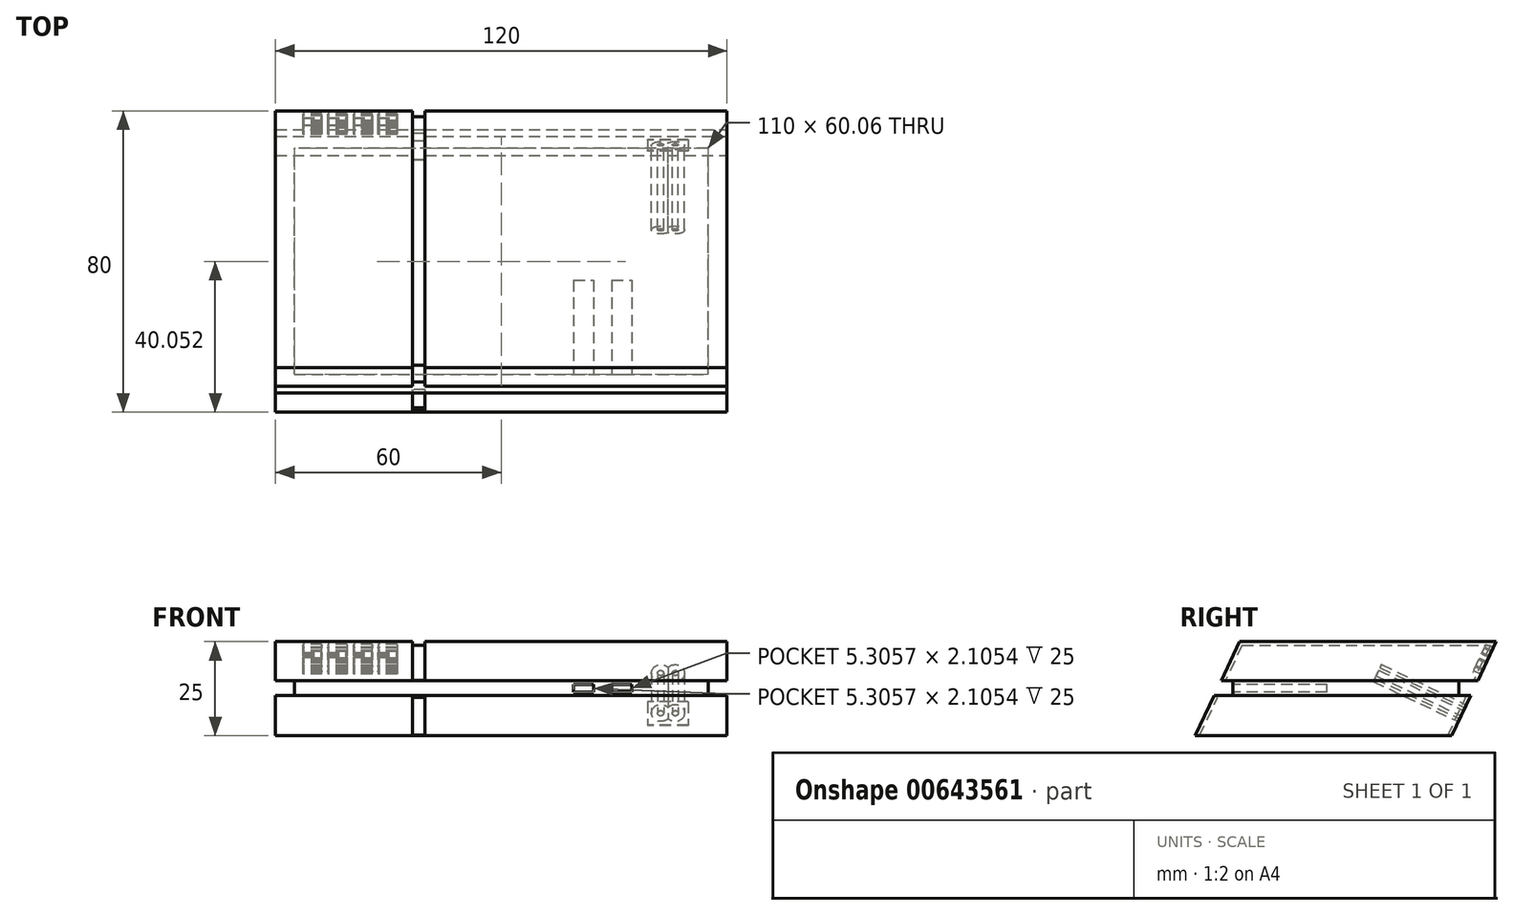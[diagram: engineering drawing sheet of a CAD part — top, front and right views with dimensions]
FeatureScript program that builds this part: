
annotation { "Feature Type Name" : "Feature", "Feature Type Description" : "" }
export const myFeature = defineFeature(function(context is Context, id is Id, definition is map)
    precondition{}
    {
        {
            var Q0;
            Q0=qCreatedBy(makeId("Top.planeOp"),FACE);
            var sketch = newSketch(context, id + "F0", { "sketchPlane" : qUnion([Q0])});
            skLineSegment(sketch, "E0.bottom", {"start": v(60, -40) * mm, "end": v(-60, -40) * mm});
            skLineSegment(sketch, "E0.top", {"start": v(60, 40) * mm, "end": v(-60, 40) * mm});
            skLineSegment(sketch, "E0.left", {"start": v(60, -40) * mm, "end": v(60, 40) * mm});
            skLineSegment(sketch, "E0.right", {"start": v(-60, -40) * mm, "end": v(-60, 40) * mm});
            skPoint(sketch, "E0.middle", {"position": v(0, 0) * mm});
            skSolve(sketch);
        }
        {
            var Q0;
            Q0=makeQuery(id+"F0.imprint","IMPRINT",FACE,{"disambiguationData":[TD([[makeQuery(id+"F0.imprint","IMPRINT",EDGE,{"derivedFrom":sQuery(id+"F0.wireOp",EDGE,"E0.bottom")}),-1.0]])]});
            extrude(context, id + "F1", {"entities" : qUnion([Q0]), "depth" : 25 * mm, "offsetDistance" : 25 * mm});
        }
        {
            var Q0;
            Q0=makeQuery(id+"F1.opExtrude","SWEPT_FACE",FACE,{"disambiguationData":[OSD([sQuery(id+"F0.wireOp",EDGE,"E0.left")])]});
            var sketch = newSketch(context, id + "F2", { "sketchPlane" : qUnion([Q0])});
            skLineSegment(sketch, "E1", {"start": v(-28.19, 25) * mm, "end": v(-40, 0) * mm});
            skSolve(sketch);
        }
        {
            var Q0;
            {var subQ0=sQuery(id+"F2.wireOp",EDGE,"E1");Q0=makeQuery(id+"F2.imprint","IMPRINT",FACE,{"disambiguationData":[TD([[makeQuery(id+"F2.imprint","IMPRINT",EDGE,{"derivedFrom":subQ0}),-1.0]])]});}
            extrude(context, id + "F3", {"entities" : qUnion([Q0]), "operationType" : NewBodyOperationType.REMOVE, "endBound" : BoundingType.THROUGH_ALL, "oppositeDirection" : true, "depth" : 25 * mm, "offsetDistance" : 25 * mm});
        }
        {
            var Q0;
            Q0=makeQuery(id+"F1.opExtrude","SWEPT_FACE",FACE,{"disambiguationData":[OSD([sQuery(id+"F0.wireOp",EDGE,"E0.left")])]});
            var sketch = newSketch(context, id + "F4", { "sketchPlane" : qUnion([Q0])});
            skLineSegment(sketch, "E2", {"start": v(40, 25) * mm, "end": v(28.19, 0) * mm});
            skSolve(sketch);
        }
        {
            var Q0;
            {var subQ0=sQuery(id+"F4.wireOp",EDGE,"E2");Q0=makeQuery(id+"F4.imprint","IMPRINT",FACE,{"disambiguationData":[TD([[makeQuery(id+"F4.imprint","IMPRINT",EDGE,{"derivedFrom":subQ0}),1.0]])]});}
            extrude(context, id + "F5", {"entities" : qUnion([Q0]), "operationType" : NewBodyOperationType.REMOVE, "endBound" : BoundingType.THROUGH_ALL, "oppositeDirection" : true, "depth" : 25 * mm, "offsetDistance" : 25 * mm});
        }
        {
            var Q0;
            Q0=makeQuery(id+"F1.opExtrude","SWEPT_FACE",FACE,{"disambiguationData":[OSD([sQuery(id+"F0.wireOp",EDGE,"E0.left")])]});
            var sketch = newSketch(context, id + "F6", { "sketchPlane" : qUnion([Q0])});
            skLineSegment(sketch, "E3.bottom", {"start": v(-40.65, 14.59) * mm, "end": v(40.65, 14.59) * mm});
            skLineSegment(sketch, "E3.top", {"start": v(-40.65, 10.62) * mm, "end": v(40.65, 10.62) * mm});
            skLineSegment(sketch, "E3.left", {"start": v(-40.65, 14.59) * mm, "end": v(-40.65, 10.62) * mm});
            skLineSegment(sketch, "E3.right", {"start": v(40.65, 14.59) * mm, "end": v(40.65, 10.62) * mm});
            skPoint(sketch, "E3.middle", {"position": v(0, 12.6) * mm});
            skSolve(sketch);
        }
        {
            var Q0;
            {var subQ0=sQuery(id+"F6.wireOp",EDGE,"E3.bottom");var subQ1=makeQuery(id+"F3.boolean.opBoolean","COPY",EDGE,{"derivedFrom":makeQuery(id+"F3.opExtrude","CAP_EDGE",EDGE,{"disambiguationData":[OSD([sQuery(id+"F2.wireOp",EDGE,"E1")])],"isStart":true})});var subQ2=makeQuery(id+"F6.imprint","INTERSECT",VERTEX,{"derivedFrom":[subQ1,subQ0]});Q0=makeQuery(id+"F6.imprint","IMPRINT",FACE,{"disambiguationData":[TD([[makeQuery(id+"F6.imprint","IMPRINT",EDGE,{"disambiguationData":[TD([[subQ2,-1.0]])],"derivedFrom":subQ0}),-1.0]])]});}
            extrude(context, id + "F7", {"entities" : qUnion([Q0]), "operationType" : NewBodyOperationType.REMOVE, "oppositeDirection" : true, "depth" : 5 * mm, "offsetDistance" : 25 * mm});
        }
        {
            var Q0;
            Q0=makeQuery(id+"F7.boolean.opBoolean","COPY",FACE,{"derivedFrom":makeQuery(id+"F7.opExtrude","CAP_FACE",FACE,{"disambiguationData":[OSD([sQuery(id+"F2.wireOp",EDGE,"E1"),sQuery(id+"F4.wireOp",EDGE,"E2"),sQuery(id+"F6.wireOp",EDGE,"E3.bottom"),sQuery(id+"F6.wireOp",EDGE,"E3.top")])],"isStart":false})});
            var sketch = newSketch(context, id + "F8", { "sketchPlane" : qUnion([Q0])});
            skLineSegment(sketch, "E4.bottom", {"start": v(-34.98, 10.62) * mm, "end": v(-29.98, 10.62) * mm});
            skLineSegment(sketch, "E4.top", {"start": v(-34.98, 14.59) * mm, "end": v(-29.98, 14.59) * mm});
            skLineSegment(sketch, "E4.left", {"start": v(-34.98, 10.62) * mm, "end": v(-34.98, 14.59) * mm});
            skLineSegment(sketch, "E4.right", {"start": v(-29.98, 10.62) * mm, "end": v(-29.98, 14.59) * mm});
            skSolve(sketch);
        }
        {
            var Q0;
            Q0=makeQuery(id+"F8.imprint","IMPRINT",FACE,{"disambiguationData":[TD([[makeQuery(id+"F8.imprint","IMPRINT",EDGE,{"derivedFrom":sQuery(id+"F8.wireOp",EDGE,"E4.bottom")}),1.0]])]});
            extrude(context, id + "F9", {"entities" : qUnion([Q0]), "operationType" : NewBodyOperationType.REMOVE, "oppositeDirection" : true, "depth" : 150 * mm, "offsetDistance" : 25 * mm});
        }
        {
            var Q0;
            Q0=makeQuery(id+"F1.opExtrude","SWEPT_FACE",FACE,{"disambiguationData":[OSD([sQuery(id+"F0.wireOp",EDGE,"E0.right")])]});
            var sketch = newSketch(context, id + "F10", { "sketchPlane" : qUnion([Q0])});
            skLineSegment(sketch, "E5.bottom", {"start": v(29.98, 14.59) * mm, "end": v(-38.1, 14.59) * mm});
            skLineSegment(sketch, "E5.top", {"start": v(29.98, 10.62) * mm, "end": v(-38.1, 10.62) * mm});
            skLineSegment(sketch, "E5.left", {"start": v(29.98, 14.59) * mm, "end": v(29.98, 10.62) * mm});
            skLineSegment(sketch, "E5.right", {"start": v(-38.1, 14.59) * mm, "end": v(-38.1, 10.62) * mm});
            skSolve(sketch);
        }
        {
            var Q0;
            {var subQ0=sQuery(id+"F10.wireOp",EDGE,"E5.left");Q0=makeQuery(id+"F10.imprint","IMPRINT",FACE,{"disambiguationData":[TD([[makeQuery(id+"F10.imprint","IMPRINT",EDGE,{"derivedFrom":subQ0}),-1.0]])]});}
            extrude(context, id + "F11", {"entities" : qUnion([Q0]), "operationType" : NewBodyOperationType.REMOVE, "oppositeDirection" : true, "depth" : 5 * mm, "offsetDistance" : 25 * mm});
        }
        {
            var Q0;
            Q0=makeQuery(id+"F11.boolean.opBoolean","COPY",FACE,{"derivedFrom":makeQuery(id+"F11.opExtrude","CAP_FACE",FACE,{"disambiguationData":[OSD([sQuery(id+"F0.wireOp",EDGE,"E0.right"),sQuery(id+"F4.wireOp",EDGE,"E2"),sQuery(id+"F10.wireOp",EDGE,"E5.bottom"),sQuery(id+"F10.wireOp",EDGE,"E5.top"),sQuery(id+"F10.wireOp",EDGE,"E5.left")])],"isStart":false})});
            var sketch = newSketch(context, id + "F12", { "sketchPlane" : qUnion([Q0])});
            skLineSegment(sketch, "E6.bottom", {"start": v(-35.08, 14.59) * mm, "end": v(-30.08, 14.59) * mm});
            skLineSegment(sketch, "E6.top", {"start": v(-35.08, 10.62) * mm, "end": v(-30.08, 10.62) * mm});
            skLineSegment(sketch, "E6.left", {"start": v(-35.08, 14.59) * mm, "end": v(-35.08, 10.62) * mm});
            skLineSegment(sketch, "E6.right", {"start": v(-30.08, 14.59) * mm, "end": v(-30.08, 10.62) * mm});
            skSolve(sketch);
        }
        {
            var Q0;
            Q0=makeQuery(id+"F12.imprint","IMPRINT",FACE,{"disambiguationData":[TD([[makeQuery(id+"F12.imprint","IMPRINT",EDGE,{"derivedFrom":sQuery(id+"F12.wireOp",EDGE,"E6.bottom")}),1.0]])]});
            extrude(context, id + "F13", {"entities" : qUnion([Q0]), "operationType" : NewBodyOperationType.REMOVE, "oppositeDirection" : true, "depth" : 170 * mm, "offsetDistance" : 25 * mm});
        }
        {
            var Q0;
            Q0=makeQuery(id+"F9.boolean.opBoolean","SPLIT",FACE,{"disambiguationData":[TD([makeQuery(id+"F7.boolean.opBoolean","COPY",FACE,{"derivedFrom":makeQuery(id+"F7.opExtrude","SWEPT_FACE",FACE,{"disambiguationData":[OSD([sQuery(id+"F6.wireOp",EDGE,"E3.bottom")])]})})])],"derivedFrom":makeQuery(id+"F3.boolean.opBoolean","COPY",FACE,{"derivedFrom":makeQuery(id+"F3.opExtrude","SWEPT_FACE",FACE,{"disambiguationData":[OSD([sQuery(id+"F2.wireOp",EDGE,"E1")])]})})});
            var sketch = newSketch(context, id + "F14", { "sketchPlane" : qUnion([Q0])});
            skLineSegment(sketch, "E7.bottom", {"start": v(-23.65, 10.56) * mm, "end": v(-20.25, 10.56) * mm});
            skLineSegment(sketch, "E7.top", {"start": v(-23.65, -0.96) * mm, "end": v(-20.25, -0.96) * mm});
            skLineSegment(sketch, "E7.left", {"start": v(-23.65, 10.56) * mm, "end": v(-23.65, -0.96) * mm});
            skLineSegment(sketch, "E7.right", {"start": v(-20.25, 10.56) * mm, "end": v(-20.25, -0.96) * mm});
            skLineSegment(sketch, "E8.bottom", {"start": v(-20.25, -16.93) * mm, "end": v(-23.65, -16.93) * mm});
            skLineSegment(sketch, "E8.top", {"start": v(-20.25, -5.34) * mm, "end": v(-23.65, -5.34) * mm});
            skLineSegment(sketch, "E8.left", {"start": v(-20.25, -16.93) * mm, "end": v(-20.25, -5.34) * mm});
            skLineSegment(sketch, "E8.right", {"start": v(-23.65, -16.93) * mm, "end": v(-23.65, -5.34) * mm});
            skSolve(sketch);
        }
        {
            var Q0;
            Q0=makeQuery(id+"F14.imprint","IMPRINT",FACE,{"disambiguationData":[TD([[makeQuery(id+"F14.imprint","IMPRINT",EDGE,{"derivedFrom":sQuery(id+"F14.wireOp",EDGE,"E7.bottom")}),-1.0]])]});
            var Q1;
            Q1=makeQuery(id+"F14.imprint","IMPRINT",FACE,{"disambiguationData":[TD([[makeQuery(id+"F14.imprint","IMPRINT",EDGE,{"derivedFrom":sQuery(id+"F14.wireOp",EDGE,"E8.bottom")}),-1.0]])]});
            extrude(context, id + "F15", {"entities" : qUnion([Q0, Q1]), "operationType" : NewBodyOperationType.REMOVE, "oppositeDirection" : true, "depth" : 1 * mm, "offsetDistance" : 25 * mm});
        }
        {
            var Q0;
            Q0=makeQuery(id+"F1.opExtrude","CAP_FACE",FACE,{"disambiguationData":[OSD([sQuery(id+"F0.wireOp",EDGE,"E0.bottom"),sQuery(id+"F0.wireOp",EDGE,"E0.top"),sQuery(id+"F0.wireOp",EDGE,"E0.left"),sQuery(id+"F0.wireOp",EDGE,"E0.right")])],"isStart":false});
            var sketch = newSketch(context, id + "F16", { "sketchPlane" : qUnion([Q0])});
            skLineSegment(sketch, "E9.bottom", {"start": v(-23.65, -28.19) * mm, "end": v(-20.25, -28.19) * mm});
            skLineSegment(sketch, "E9.top", {"start": v(-23.65, 40) * mm, "end": v(-20.25, 40) * mm});
            skLineSegment(sketch, "E9.left", {"start": v(-23.65, -28.19) * mm, "end": v(-23.65, 40) * mm});
            skLineSegment(sketch, "E9.right", {"start": v(-20.25, -28.19) * mm, "end": v(-20.25, 40) * mm});
            skSolve(sketch);
        }
        {
            var Q0;
            Q0=makeQuery(id+"F16.imprint","IMPRINT",FACE,{"disambiguationData":[TD([[makeQuery(id+"F16.imprint","IMPRINT",EDGE,{"derivedFrom":sQuery(id+"F16.wireOp",EDGE,"E9.bottom")}),1.0]])]});
            extrude(context, id + "F17", {"entities" : qUnion([Q0]), "operationType" : NewBodyOperationType.REMOVE, "oppositeDirection" : true, "depth" : 1 * mm, "offsetDistance" : 25 * mm});
        }
        {
            var Q0;
            Q0=makeQuery(id+"F13.boolean.opBoolean","SPLIT",FACE,{"disambiguationData":[TD([makeQuery(id+"F7.boolean.opBoolean","COPY",FACE,{"derivedFrom":makeQuery(id+"F7.opExtrude","SWEPT_FACE",FACE,{"disambiguationData":[OSD([sQuery(id+"F6.wireOp",EDGE,"E3.bottom")])]})})])],"derivedFrom":makeQuery(id+"F5.boolean.opBoolean","COPY",FACE,{"derivedFrom":makeQuery(id+"F5.opExtrude","SWEPT_FACE",FACE,{"disambiguationData":[OSD([sQuery(id+"F4.wireOp",EDGE,"E2")])]})})});
            var sketch = newSketch(context, id + "F18", { "sketchPlane" : qUnion([Q0])});
            skLineSegment(sketch, "E10.bottom", {"start": v(20.25, 39.7) * mm, "end": v(23.65, 39.7) * mm});
            skLineSegment(sketch, "E10.top", {"start": v(20.25, 28.18) * mm, "end": v(23.65, 28.18) * mm});
            skLineSegment(sketch, "E10.left", {"start": v(20.25, 39.7) * mm, "end": v(20.25, 28.18) * mm});
            skLineSegment(sketch, "E10.right", {"start": v(23.65, 39.7) * mm, "end": v(23.65, 28.18) * mm});
            skLineSegment(sketch, "E11.bottom", {"start": v(23.65, 11.57) * mm, "end": v(20.25, 11.57) * mm});
            skLineSegment(sketch, "E11.top", {"start": v(23.65, 23.8) * mm, "end": v(20.25, 23.8) * mm});
            skLineSegment(sketch, "E11.left", {"start": v(23.65, 11.57) * mm, "end": v(23.65, 23.8) * mm});
            skLineSegment(sketch, "E11.right", {"start": v(20.25, 11.57) * mm, "end": v(20.25, 23.8) * mm});
            skSolve(sketch);
        }
        {
            var Q0;
            {var subQ0=sQuery(id+"F18.wireOp",EDGE,"E10.top");Q0=makeQuery(id+"F18.imprint","IMPRINT",FACE,{"disambiguationData":[TD([[makeQuery(id+"F18.imprint","IMPRINT",EDGE,{"derivedFrom":subQ0}),-1.0]])]});}
            var Q1;
            Q1=makeQuery(id+"F18.imprint","IMPRINT",FACE,{"disambiguationData":[TD([[makeQuery(id+"F18.imprint","IMPRINT",EDGE,{"derivedFrom":sQuery(id+"F18.wireOp",EDGE,"E11.bottom")}),-1.0]])]});
            extrude(context, id + "F19", {"entities" : qUnion([Q0, Q1]), "operationType" : NewBodyOperationType.REMOVE, "oppositeDirection" : true, "depth" : 1 * mm, "offsetDistance" : 25 * mm});
        }
        {
            var Q0;
            Q0=makeQuery(id+"F9.boolean.opBoolean","COPY",FACE,{"derivedFrom":makeQuery(id+"F9.opExtrude","SWEPT_FACE",FACE,{"disambiguationData":[OSD([sQuery(id+"F8.wireOp",EDGE,"E4.right")])]})});
            var sketch = newSketch(context, id + "F20", { "sketchPlane" : qUnion([Q0])});
            skLineSegment(sketch, "E12.bottom", {"start": v(19.23, 13.64) * mm, "end": v(24.53, 13.64) * mm});
            skLineSegment(sketch, "E12.top", {"start": v(19.23, 11.53) * mm, "end": v(24.53, 11.53) * mm});
            skLineSegment(sketch, "E12.left", {"start": v(19.23, 13.64) * mm, "end": v(19.23, 11.53) * mm});
            skLineSegment(sketch, "E12.right", {"start": v(24.53, 13.64) * mm, "end": v(24.53, 11.53) * mm});
            skLineSegment(sketch, "E13.bottom", {"start": v(29.42, 11.53) * mm, "end": v(34.72, 11.53) * mm});
            skLineSegment(sketch, "E13.top", {"start": v(29.42, 13.64) * mm, "end": v(34.72, 13.64) * mm});
            skLineSegment(sketch, "E13.left", {"start": v(29.42, 11.53) * mm, "end": v(29.42, 13.64) * mm});
            skLineSegment(sketch, "E13.right", {"start": v(34.72, 11.53) * mm, "end": v(34.72, 13.64) * mm});
            skSolve(sketch);
        }
        {
            var Q0;
            Q0=makeQuery(id+"F20.imprint","IMPRINT",FACE,{"disambiguationData":[TD([[makeQuery(id+"F20.imprint","IMPRINT",EDGE,{"derivedFrom":sQuery(id+"F20.wireOp",EDGE,"E12.bottom")}),-1.0]])]});
            var Q1;
            Q1=makeQuery(id+"F20.imprint","IMPRINT",FACE,{"disambiguationData":[TD([[makeQuery(id+"F20.imprint","IMPRINT",EDGE,{"derivedFrom":sQuery(id+"F20.wireOp",EDGE,"E13.bottom")}),1.0]])]});
            extrude(context, id + "F21", {"entities" : qUnion([Q0, Q1]), "operationType" : NewBodyOperationType.REMOVE, "oppositeDirection" : true, "depth" : 25 * mm, "offsetDistance" : 25 * mm});
        }
        {
            var Q0;
            {var subQ1=makeQuery(id+"F7.boolean.opBoolean","COPY",FACE,{"derivedFrom":makeQuery(id+"F7.opExtrude","SWEPT_FACE",FACE,{"disambiguationData":[OSD([sQuery(id+"F6.wireOp",EDGE,"E3.top")])]})});var subQ2=sQuery(id+"F0.wireOp",EDGE,"E0.left");var subQ3=makeQuery(id+"F1.opExtrude","SWEPT_FACE",FACE,{"disambiguationData":[OSD([subQ2])]});Q0=makeQuery(id+"F19.boolean.opBoolean","SPLIT",FACE,{"disambiguationData":[TD([subQ3])],"derivedFrom":makeQuery(id+"F13.boolean.opBoolean","SPLIT",FACE,{"disambiguationData":[TD([subQ1])],"derivedFrom":makeQuery(id+"F5.boolean.opBoolean","COPY",FACE,{"derivedFrom":makeQuery(id+"F5.opExtrude","SWEPT_FACE",FACE,{"disambiguationData":[OSD([sQuery(id+"F4.wireOp",EDGE,"E2")])]})})})});}
            var sketch = newSketch(context, id + "F22", { "sketchPlane" : qUnion([Q0])});
            skCircle(sketch, "E14", {"center": v(-46.22, 18.61) * mm, "radius": 2.5 * mm});
            skCircle(sketch, "E15", {"center": v(-42.41, 18.61) * mm, "radius": 2.5 * mm});
            skSolve(sketch);
        }
        {
            var Q0;
            {var subQ0=sQuery(id+"F22.wireOp",EDGE,"E15");var subQ1=sQuery(id+"F22.wireOp",EDGE,"E14");var subQ2=makeQuery(id+"F22.imprint","INTERSECT",VERTEX,{"disambiguationData":[OD(0.0)],"derivedFrom":[subQ1,subQ0]});Q0=makeQuery(id+"F22.imprint","IMPRINT",FACE,{"disambiguationData":[TD([[makeQuery(id+"F22.imprint","IMPRINT",EDGE,{"disambiguationData":[TD([[subQ2,-1.0]])],"derivedFrom":subQ1}),-1.0]])]});}
            var sketch = newSketch(context, id + "F23", { "sketchPlane" : qUnion([Q0])});
            skCircle(sketch, "E16", {"center": v(-42.36, 18.65) * mm, "radius": 0.79 * mm});
            skCircle(sketch, "E17", {"center": v(-46.28, 18.65) * mm, "radius": 0.79 * mm});
            skSolve(sketch);
        }
        {
            var Q0;
            {var subQ0=sQuery(id+"F22.wireOp",EDGE,"E15");var subQ1=sQuery(id+"F22.wireOp",EDGE,"E14");var subQ2=makeQuery(id+"F22.imprint","INTERSECT",VERTEX,{"disambiguationData":[OD(0.0)],"derivedFrom":[subQ1,subQ0]});Q0=makeQuery(id+"F22.imprint","IMPRINT",FACE,{"disambiguationData":[TD([[makeQuery(id+"F22.imprint","IMPRINT",EDGE,{"disambiguationData":[TD([[subQ2,-1.0]])],"derivedFrom":subQ1}),1.0]])]});}
            var Q1;
            {var subQ0=sQuery(id+"F22.wireOp",EDGE,"E15");var subQ1=sQuery(id+"F22.wireOp",EDGE,"E14");var subQ2=makeQuery(id+"F22.imprint","INTERSECT",VERTEX,{"disambiguationData":[OD(0.0)],"derivedFrom":[subQ1,subQ0]});Q1=makeQuery(id+"F22.imprint","IMPRINT",FACE,{"disambiguationData":[TD([[makeQuery(id+"F22.imprint","IMPRINT",EDGE,{"disambiguationData":[TD([[subQ2,1.0]])],"derivedFrom":subQ1}),1.0]])]});}
            var Q2;
            {var subQ0=sQuery(id+"F22.wireOp",EDGE,"E15");var subQ1=sQuery(id+"F22.wireOp",EDGE,"E14");var subQ2=makeQuery(id+"F22.imprint","INTERSECT",VERTEX,{"disambiguationData":[OD(0.0)],"derivedFrom":[subQ1,subQ0]});Q2=makeQuery(id+"F22.imprint","IMPRINT",FACE,{"disambiguationData":[TD([[makeQuery(id+"F22.imprint","IMPRINT",EDGE,{"disambiguationData":[TD([[subQ2,-1.0]])],"derivedFrom":subQ1}),-1.0]])]});}
            extrude(context, id + "F24", {"entities" : qUnion([Q0, Q1, Q2]), "operationType" : NewBodyOperationType.REMOVE, "oppositeDirection" : true, "depth" : 25 * mm, "offsetDistance" : 25 * mm});
        }
        {
            var Q0;
            Q0=makeQuery(id+"F23.imprint","IMPRINT",FACE,{"disambiguationData":[TD([[makeQuery(id+"F23.imprint","IMPRINT",EDGE,{"derivedFrom":sQuery(id+"F23.wireOp",EDGE,"E16")}),1.0]])]});
            var Q1;
            Q1=makeQuery(id+"F23.imprint","IMPRINT",FACE,{"disambiguationData":[TD([[makeQuery(id+"F23.imprint","IMPRINT",EDGE,{"derivedFrom":sQuery(id+"F23.wireOp",EDGE,"E17")}),1.0]])]});
            extrude(context, id + "F25", {"entities" : qUnion([Q0, Q1]), "operationType" : NewBodyOperationType.ADD, "oppositeDirection" : true, "depth" : 25 * mm, "offsetDistance" : 25 * mm});
        }
        {
            var Q0;
            {var subQ1=makeQuery(id+"F7.boolean.opBoolean","COPY",FACE,{"derivedFrom":makeQuery(id+"F7.opExtrude","SWEPT_FACE",FACE,{"disambiguationData":[OSD([sQuery(id+"F6.wireOp",EDGE,"E3.top")])]})});var subQ2=sQuery(id+"F0.wireOp",EDGE,"E0.left");var subQ3=makeQuery(id+"F1.opExtrude","SWEPT_FACE",FACE,{"disambiguationData":[OSD([subQ2])]});Q0=makeQuery(id+"F19.boolean.opBoolean","SPLIT",FACE,{"disambiguationData":[TD([subQ3])],"derivedFrom":makeQuery(id+"F13.boolean.opBoolean","SPLIT",FACE,{"disambiguationData":[TD([subQ1])],"derivedFrom":makeQuery(id+"F5.boolean.opBoolean","COPY",FACE,{"derivedFrom":makeQuery(id+"F5.opExtrude","SWEPT_FACE",FACE,{"disambiguationData":[OSD([sQuery(id+"F4.wireOp",EDGE,"E2")])]})})})});}
            var sketch = newSketch(context, id + "F26", { "sketchPlane" : qUnion([Q0])});
            skLineSegment(sketch, "E18.bottom", {"start": v(-49.72, 22) * mm, "end": v(-38.92, 22) * mm});
            skLineSegment(sketch, "E18.top", {"start": v(-49.72, 15.01) * mm, "end": v(-38.92, 15.01) * mm});
            skLineSegment(sketch, "E18.left", {"start": v(-49.72, 22) * mm, "end": v(-49.72, 15.01) * mm});
            skLineSegment(sketch, "E18.right", {"start": v(-38.92, 22) * mm, "end": v(-38.92, 15.01) * mm});
            skPoint(sketch, "E18.middle", {"position": v(-44.32, 18.5) * mm});
            skSolve(sketch);
        }
        {
            var Q0;
            Q0=makeQuery(id+"F26.imprint","IMPRINT",FACE,{"disambiguationData":[TD([[makeQuery(id+"F26.imprint","IMPRINT",EDGE,{"derivedFrom":sQuery(id+"F26.wireOp",EDGE,"E18.bottom")}),-1.0]])]});
            extrude(context, id + "F27", {"entities" : qUnion([Q0]), "operationType" : NewBodyOperationType.REMOVE, "oppositeDirection" : true, "depth" : 0.2 * mm, "offsetDistance" : 25 * mm});
        }
        {
            var Q0;
            {var subQ1=makeQuery(id+"F7.boolean.opBoolean","COPY",FACE,{"derivedFrom":makeQuery(id+"F7.opExtrude","SWEPT_FACE",FACE,{"disambiguationData":[OSD([sQuery(id+"F6.wireOp",EDGE,"E3.top")])]})});var subQ2=sQuery(id+"F0.wireOp",EDGE,"E0.left");var subQ3=makeQuery(id+"F1.opExtrude","SWEPT_FACE",FACE,{"disambiguationData":[OSD([subQ2])]});Q0=makeQuery(id+"F19.boolean.opBoolean","SPLIT",FACE,{"disambiguationData":[TD([subQ3])],"derivedFrom":makeQuery(id+"F13.boolean.opBoolean","SPLIT",FACE,{"disambiguationData":[TD([subQ1])],"derivedFrom":makeQuery(id+"F5.boolean.opBoolean","COPY",FACE,{"derivedFrom":makeQuery(id+"F5.opExtrude","SWEPT_FACE",FACE,{"disambiguationData":[OSD([sQuery(id+"F4.wireOp",EDGE,"E2")])]})})})});}
            var sketch = newSketch(context, id + "F28", { "sketchPlane" : qUnion([Q0])});
            skLineSegment(sketch, "E19.bottom", {"start": v(27.68, 37.89) * mm, "end": v(32.68, 37.89) * mm});
            skLineSegment(sketch, "E19.top", {"start": v(27.68, 29.74) * mm, "end": v(32.68, 29.74) * mm});
            skLineSegment(sketch, "E19.left", {"start": v(27.68, 37.89) * mm, "end": v(27.68, 29.74) * mm});
            skLineSegment(sketch, "E19.right", {"start": v(32.68, 37.89) * mm, "end": v(32.68, 29.74) * mm});
            skLineSegment(sketch, "E20.bottom", {"start": v(34.26, 29.74) * mm, "end": v(39.26, 29.74) * mm});
            skLineSegment(sketch, "E20.top", {"start": v(34.26, 37.89) * mm, "end": v(39.26, 37.89) * mm});
            skLineSegment(sketch, "E20.left", {"start": v(34.26, 29.74) * mm, "end": v(34.26, 37.89) * mm});
            skLineSegment(sketch, "E20.right", {"start": v(39.26, 29.74) * mm, "end": v(39.26, 37.89) * mm});
            skLineSegment(sketch, "E21.bottom", {"start": v(41.05, 37.89) * mm, "end": v(46.05, 37.89) * mm});
            skLineSegment(sketch, "E21.top", {"start": v(41.05, 29.74) * mm, "end": v(46.05, 29.74) * mm});
            skLineSegment(sketch, "E21.left", {"start": v(41.05, 37.89) * mm, "end": v(41.05, 29.74) * mm});
            skLineSegment(sketch, "E21.right", {"start": v(46.05, 37.89) * mm, "end": v(46.05, 29.74) * mm});
            skLineSegment(sketch, "E22.bottom", {"start": v(47.68, 29.74) * mm, "end": v(52.68, 29.74) * mm});
            skLineSegment(sketch, "E22.top", {"start": v(47.68, 37.89) * mm, "end": v(52.68, 37.89) * mm});
            skLineSegment(sketch, "E22.left", {"start": v(47.68, 29.74) * mm, "end": v(47.68, 37.89) * mm});
            skLineSegment(sketch, "E22.right", {"start": v(52.68, 29.74) * mm, "end": v(52.68, 37.89) * mm});
            skSolve(sketch);
        }
        {
            var Q0;
            Q0=makeQuery(id+"F28.imprint","IMPRINT",FACE,{"disambiguationData":[TD([[makeQuery(id+"F28.imprint","IMPRINT",EDGE,{"derivedFrom":sQuery(id+"F28.wireOp",EDGE,"E22.bottom")}),1.0]])]});
            var Q1;
            Q1=makeQuery(id+"F28.imprint","IMPRINT",FACE,{"disambiguationData":[TD([[makeQuery(id+"F28.imprint","IMPRINT",EDGE,{"derivedFrom":sQuery(id+"F28.wireOp",EDGE,"E21.bottom")}),-1.0]])]});
            var Q2;
            Q2=makeQuery(id+"F28.imprint","IMPRINT",FACE,{"disambiguationData":[TD([[makeQuery(id+"F28.imprint","IMPRINT",EDGE,{"derivedFrom":sQuery(id+"F28.wireOp",EDGE,"E20.bottom")}),1.0]])]});
            var Q3;
            Q3=makeQuery(id+"F28.imprint","IMPRINT",FACE,{"disambiguationData":[TD([[makeQuery(id+"F28.imprint","IMPRINT",EDGE,{"derivedFrom":sQuery(id+"F28.wireOp",EDGE,"E19.bottom")}),-1.0]])]});
            extrude(context, id + "F29", {"entities" : qUnion([Q0, Q1, Q2, Q3]), "operationType" : NewBodyOperationType.REMOVE, "oppositeDirection" : true, "depth" : 2.2 * mm, "offsetDistance" : 25 * mm});
        }
        {
            var Q0;
            {var subQ1=sQuery(id+"F0.wireOp",EDGE,"E0.right");var subQ2=makeQuery(id+"F1.opExtrude","SWEPT_FACE",FACE,{"disambiguationData":[OSD([subQ1])]});var subQ3=makeQuery(id+"F7.boolean.opBoolean","COPY",FACE,{"derivedFrom":makeQuery(id+"F7.opExtrude","SWEPT_FACE",FACE,{"disambiguationData":[OSD([sQuery(id+"F6.wireOp",EDGE,"E3.bottom")])]})});Q0=makeQuery(id+"F19.boolean.opBoolean","SPLIT",FACE,{"disambiguationData":[TD([subQ2])],"derivedFrom":makeQuery(id+"F13.boolean.opBoolean","SPLIT",FACE,{"disambiguationData":[TD([subQ3])],"derivedFrom":makeQuery(id+"F5.boolean.opBoolean","COPY",FACE,{"derivedFrom":makeQuery(id+"F5.opExtrude","SWEPT_FACE",FACE,{"disambiguationData":[OSD([sQuery(id+"F4.wireOp",EDGE,"E2")])]})})})});}
            var sketch = newSketch(context, id + "F30", { "sketchPlane" : qUnion([Q0])});
            skLineSegment(sketch, "E23.bottom", {"start": v(27.68, 37.12) * mm, "end": v(52.68, 37.12) * mm});
            skLineSegment(sketch, "E23.top", {"start": v(27.68, 36.72) * mm, "end": v(52.68, 36.72) * mm});
            skLineSegment(sketch, "E23.left", {"start": v(27.68, 37.12) * mm, "end": v(27.68, 36.72) * mm});
            skLineSegment(sketch, "E23.right", {"start": v(52.68, 37.12) * mm, "end": v(52.68, 36.72) * mm});
            skLineSegment(sketch, "E24.bottom", {"start": v(52.68, 35.55) * mm, "end": v(27.68, 35.55) * mm});
            skLineSegment(sketch, "E24.top", {"start": v(52.68, 35.15) * mm, "end": v(27.68, 35.15) * mm});
            skLineSegment(sketch, "E24.left", {"start": v(52.68, 35.55) * mm, "end": v(52.68, 35.15) * mm});
            skLineSegment(sketch, "E24.right", {"start": v(27.68, 35.55) * mm, "end": v(27.68, 35.15) * mm});
            skLineSegment(sketch, "E25.bottom", {"start": v(27.68, 33.81) * mm, "end": v(52.68, 33.81) * mm});
            skLineSegment(sketch, "E25.top", {"start": v(27.68, 33.41) * mm, "end": v(52.68, 33.41) * mm});
            skLineSegment(sketch, "E25.left", {"start": v(27.68, 33.81) * mm, "end": v(27.68, 33.41) * mm});
            skLineSegment(sketch, "E25.right", {"start": v(52.68, 33.81) * mm, "end": v(52.68, 33.41) * mm});
            skLineSegment(sketch, "E26.bottom", {"start": v(27.68, 31.71) * mm, "end": v(52.68, 31.71) * mm});
            skLineSegment(sketch, "E26.top", {"start": v(27.68, 31.31) * mm, "end": v(52.68, 31.31) * mm});
            skLineSegment(sketch, "E26.left", {"start": v(27.68, 31.71) * mm, "end": v(27.68, 31.31) * mm});
            skLineSegment(sketch, "E26.right", {"start": v(52.68, 31.71) * mm, "end": v(52.68, 31.31) * mm});
            skLineSegment(sketch, "E27.bottom", {"start": v(27.68, 29.74) * mm, "end": v(52.68, 29.74) * mm});
            skLineSegment(sketch, "E27.top", {"start": v(27.68, 30.14) * mm, "end": v(52.68, 30.14) * mm});
            skLineSegment(sketch, "E27.left", {"start": v(27.68, 29.74) * mm, "end": v(27.68, 30.14) * mm});
            skLineSegment(sketch, "E27.right", {"start": v(52.68, 29.74) * mm, "end": v(52.68, 30.14) * mm});
            skSolve(sketch);
        }
        {
            var Q0;
            {var subQ0=sQuery(id+"F30.wireOp",EDGE,"E23.right");Q0=makeQuery(id+"F30.imprint","IMPRINT",FACE,{"disambiguationData":[TD([[makeQuery(id+"F30.imprint","IMPRINT",EDGE,{"derivedFrom":subQ0}),1.0]])]});}
            var Q1;
            {var subQ0=sQuery(id+"F30.wireOp",EDGE,"E23.bottom");var subQ1=makeQuery(id+"F29.boolean.opBoolean","COPY",EDGE,{"derivedFrom":makeQuery(id+"F29.opExtrude","CAP_EDGE",EDGE,{"disambiguationData":[OSD([sQuery(id+"F28.wireOp",EDGE,"E21.left")])],"isStart":true})});var subQ2=makeQuery(id+"F30.imprint","INTERSECT",VERTEX,{"derivedFrom":[subQ1,subQ0]});Q1=makeQuery(id+"F30.imprint","IMPRINT",FACE,{"disambiguationData":[TD([[makeQuery(id+"F30.imprint","IMPRINT",EDGE,{"disambiguationData":[TD([[subQ2,-1.0]])],"derivedFrom":subQ0}),-1.0]])]});}
            var Q2;
            {var subQ0=sQuery(id+"F30.wireOp",EDGE,"E24.left");Q2=makeQuery(id+"F30.imprint","IMPRINT",FACE,{"disambiguationData":[TD([[makeQuery(id+"F30.imprint","IMPRINT",EDGE,{"derivedFrom":subQ0}),1.0]])]});}
            var Q3;
            {var subQ0=sQuery(id+"F30.wireOp",EDGE,"E24.bottom");var subQ1=makeQuery(id+"F29.boolean.opBoolean","COPY",EDGE,{"derivedFrom":makeQuery(id+"F29.opExtrude","CAP_EDGE",EDGE,{"disambiguationData":[OSD([sQuery(id+"F28.wireOp",EDGE,"E21.right")])],"isStart":true})});var subQ2=makeQuery(id+"F30.imprint","INTERSECT",VERTEX,{"derivedFrom":[subQ1,subQ0]});Q3=makeQuery(id+"F30.imprint","IMPRINT",FACE,{"disambiguationData":[TD([[makeQuery(id+"F30.imprint","IMPRINT",EDGE,{"disambiguationData":[TD([[subQ2,-1.0]])],"derivedFrom":subQ0}),1.0]])]});}
            var Q4;
            {var subQ0=sQuery(id+"F30.wireOp",EDGE,"E25.bottom");var subQ1=makeQuery(id+"F29.boolean.opBoolean","COPY",EDGE,{"derivedFrom":makeQuery(id+"F29.opExtrude","CAP_EDGE",EDGE,{"disambiguationData":[OSD([sQuery(id+"F28.wireOp",EDGE,"E21.left")])],"isStart":true})});var subQ2=makeQuery(id+"F30.imprint","INTERSECT",VERTEX,{"derivedFrom":[subQ1,subQ0]});Q4=makeQuery(id+"F30.imprint","IMPRINT",FACE,{"disambiguationData":[TD([[makeQuery(id+"F30.imprint","IMPRINT",EDGE,{"disambiguationData":[TD([[subQ2,-1.0]])],"derivedFrom":subQ0}),-1.0]])]});}
            var Q5;
            {var subQ0=sQuery(id+"F30.wireOp",EDGE,"E25.right");Q5=makeQuery(id+"F30.imprint","IMPRINT",FACE,{"disambiguationData":[TD([[makeQuery(id+"F30.imprint","IMPRINT",EDGE,{"derivedFrom":subQ0}),1.0]])]});}
            var Q6;
            {var subQ0=sQuery(id+"F30.wireOp",EDGE,"E26.right");Q6=makeQuery(id+"F30.imprint","IMPRINT",FACE,{"disambiguationData":[TD([[makeQuery(id+"F30.imprint","IMPRINT",EDGE,{"derivedFrom":subQ0}),1.0]])]});}
            var Q7;
            {var subQ0=sQuery(id+"F30.wireOp",EDGE,"E26.bottom");var subQ1=makeQuery(id+"F29.boolean.opBoolean","COPY",EDGE,{"derivedFrom":makeQuery(id+"F29.opExtrude","CAP_EDGE",EDGE,{"disambiguationData":[OSD([sQuery(id+"F28.wireOp",EDGE,"E21.left")])],"isStart":true})});var subQ2=makeQuery(id+"F30.imprint","INTERSECT",VERTEX,{"derivedFrom":[subQ1,subQ0]});Q7=makeQuery(id+"F30.imprint","IMPRINT",FACE,{"disambiguationData":[TD([[makeQuery(id+"F30.imprint","IMPRINT",EDGE,{"disambiguationData":[TD([[subQ2,-1.0]])],"derivedFrom":subQ0}),-1.0]])]});}
            var Q8;
            {var subQ0=sQuery(id+"F30.wireOp",EDGE,"E27.bottom");var subQ1=makeQuery(id+"F29.boolean.opBoolean","COPY",EDGE,{"derivedFrom":makeQuery(id+"F29.opExtrude","CAP_EDGE",EDGE,{"disambiguationData":[OSD([sQuery(id+"F28.wireOp",EDGE,"E21.left")])],"isStart":true})});var subQ2=makeQuery(id+"F30.imprint","INTERSECT",VERTEX,{"derivedFrom":[subQ1,subQ0]});Q8=makeQuery(id+"F30.imprint","IMPRINT",FACE,{"disambiguationData":[TD([[makeQuery(id+"F30.imprint","IMPRINT",EDGE,{"disambiguationData":[TD([[subQ2,-1.0]])],"derivedFrom":subQ0}),1.0]])]});}
            var Q9;
            {var subQ3=sQuery(id+"F30.wireOp",EDGE,"E27.right");Q9=makeQuery(id+"F30.imprint","IMPRINT",FACE,{"disambiguationData":[TD([[makeQuery(id+"F30.imprint","IMPRINT",EDGE,{"derivedFrom":subQ3}),1.0]])]});}
            var Q10;
            {var subQ0=sQuery(id+"F30.wireOp",EDGE,"E23.left");Q10=makeQuery(id+"F30.imprint","IMPRINT",FACE,{"disambiguationData":[TD([[makeQuery(id+"F30.imprint","IMPRINT",EDGE,{"derivedFrom":subQ0}),1.0]])]});}
            var Q11;
            {var subQ0=sQuery(id+"F30.wireOp",EDGE,"E23.bottom");var subQ1=makeQuery(id+"F29.boolean.opBoolean","COPY",EDGE,{"derivedFrom":makeQuery(id+"F29.opExtrude","CAP_EDGE",EDGE,{"disambiguationData":[OSD([sQuery(id+"F28.wireOp",EDGE,"E20.left")])],"isStart":true})});var subQ2=makeQuery(id+"F30.imprint","INTERSECT",VERTEX,{"derivedFrom":[subQ1,subQ0]});Q11=makeQuery(id+"F30.imprint","IMPRINT",FACE,{"disambiguationData":[TD([[makeQuery(id+"F30.imprint","IMPRINT",EDGE,{"disambiguationData":[TD([[subQ2,-1.0]])],"derivedFrom":subQ0}),-1.0]])]});}
            var Q12;
            {var subQ0=sQuery(id+"F30.wireOp",EDGE,"E24.bottom");var subQ1=makeQuery(id+"F29.boolean.opBoolean","COPY",EDGE,{"derivedFrom":makeQuery(id+"F29.opExtrude","CAP_EDGE",EDGE,{"disambiguationData":[OSD([sQuery(id+"F28.wireOp",EDGE,"E20.right")])],"isStart":true})});var subQ2=makeQuery(id+"F30.imprint","INTERSECT",VERTEX,{"derivedFrom":[subQ1,subQ0]});Q12=makeQuery(id+"F30.imprint","IMPRINT",FACE,{"disambiguationData":[TD([[makeQuery(id+"F30.imprint","IMPRINT",EDGE,{"disambiguationData":[TD([[subQ2,-1.0]])],"derivedFrom":subQ0}),1.0]])]});}
            var Q13;
            {var subQ0=sQuery(id+"F30.wireOp",EDGE,"E24.right");Q13=makeQuery(id+"F30.imprint","IMPRINT",FACE,{"disambiguationData":[TD([[makeQuery(id+"F30.imprint","IMPRINT",EDGE,{"derivedFrom":subQ0}),1.0]])]});}
            var Q14;
            {var subQ0=sQuery(id+"F30.wireOp",EDGE,"E25.left");Q14=makeQuery(id+"F30.imprint","IMPRINT",FACE,{"disambiguationData":[TD([[makeQuery(id+"F30.imprint","IMPRINT",EDGE,{"derivedFrom":subQ0}),1.0]])]});}
            var Q15;
            {var subQ0=sQuery(id+"F30.wireOp",EDGE,"E25.bottom");var subQ1=makeQuery(id+"F29.boolean.opBoolean","COPY",EDGE,{"derivedFrom":makeQuery(id+"F29.opExtrude","CAP_EDGE",EDGE,{"disambiguationData":[OSD([sQuery(id+"F28.wireOp",EDGE,"E20.left")])],"isStart":true})});var subQ2=makeQuery(id+"F30.imprint","INTERSECT",VERTEX,{"derivedFrom":[subQ1,subQ0]});Q15=makeQuery(id+"F30.imprint","IMPRINT",FACE,{"disambiguationData":[TD([[makeQuery(id+"F30.imprint","IMPRINT",EDGE,{"disambiguationData":[TD([[subQ2,-1.0]])],"derivedFrom":subQ0}),-1.0]])]});}
            var Q16;
            {var subQ0=sQuery(id+"F30.wireOp",EDGE,"E26.left");Q16=makeQuery(id+"F30.imprint","IMPRINT",FACE,{"disambiguationData":[TD([[makeQuery(id+"F30.imprint","IMPRINT",EDGE,{"derivedFrom":subQ0}),1.0]])]});}
            var Q17;
            {var subQ0=sQuery(id+"F30.wireOp",EDGE,"E26.bottom");var subQ1=makeQuery(id+"F29.boolean.opBoolean","COPY",EDGE,{"derivedFrom":makeQuery(id+"F29.opExtrude","CAP_EDGE",EDGE,{"disambiguationData":[OSD([sQuery(id+"F28.wireOp",EDGE,"E20.left")])],"isStart":true})});var subQ2=makeQuery(id+"F30.imprint","INTERSECT",VERTEX,{"derivedFrom":[subQ1,subQ0]});Q17=makeQuery(id+"F30.imprint","IMPRINT",FACE,{"disambiguationData":[TD([[makeQuery(id+"F30.imprint","IMPRINT",EDGE,{"disambiguationData":[TD([[subQ2,-1.0]])],"derivedFrom":subQ0}),-1.0]])]});}
            var Q18;
            {var subQ0=sQuery(id+"F30.wireOp",EDGE,"E27.left");Q18=makeQuery(id+"F30.imprint","IMPRINT",FACE,{"disambiguationData":[TD([[makeQuery(id+"F30.imprint","IMPRINT",EDGE,{"derivedFrom":subQ0}),1.0]])]});}
            var Q19;
            {var subQ0=sQuery(id+"F30.wireOp",EDGE,"E27.bottom");var subQ1=makeQuery(id+"F29.boolean.opBoolean","COPY",EDGE,{"derivedFrom":makeQuery(id+"F29.opExtrude","CAP_EDGE",EDGE,{"disambiguationData":[OSD([sQuery(id+"F28.wireOp",EDGE,"E20.left")])],"isStart":true})});var subQ2=makeQuery(id+"F30.imprint","INTERSECT",VERTEX,{"derivedFrom":[subQ1,subQ0]});Q19=makeQuery(id+"F30.imprint","IMPRINT",FACE,{"disambiguationData":[TD([[makeQuery(id+"F30.imprint","IMPRINT",EDGE,{"disambiguationData":[TD([[subQ2,-1.0]])],"derivedFrom":subQ0}),1.0]])]});}
            extrude(context, id + "F31", {"entities" : qUnion([Q0, Q1, Q2, Q3, Q4, Q5, Q6, Q7, Q8, Q9, Q10, Q11, Q12, Q13, Q14, Q15, Q16, Q17, Q18, Q19]), "operationType" : NewBodyOperationType.ADD, "oppositeDirection" : true, "depth" : 2.1 * mm, "offsetDistance" : 25 * mm});
        }
    });
